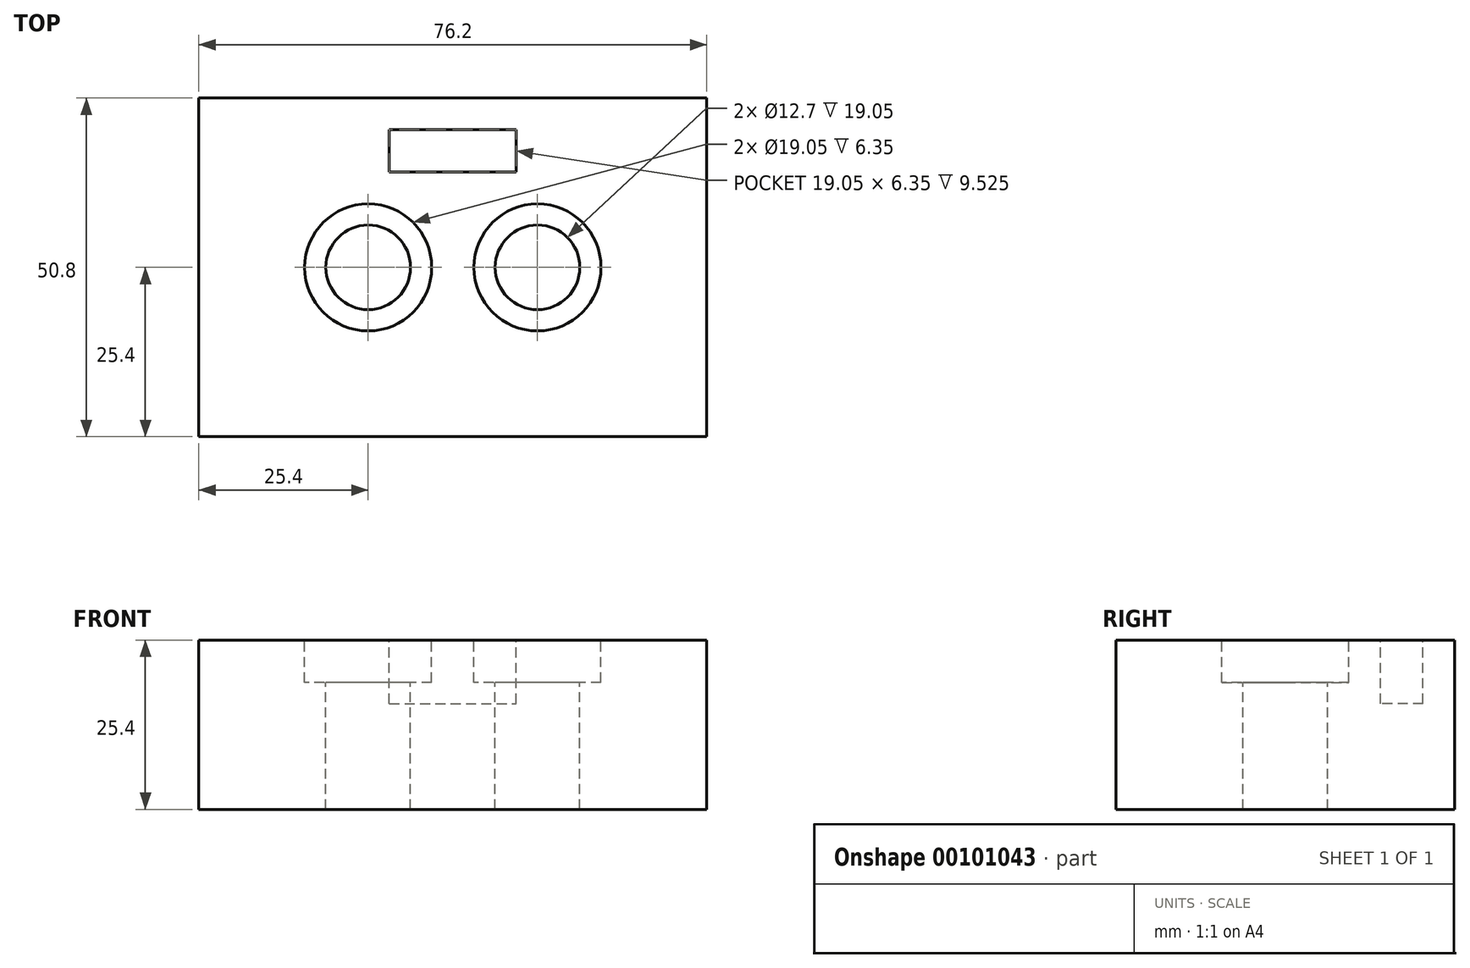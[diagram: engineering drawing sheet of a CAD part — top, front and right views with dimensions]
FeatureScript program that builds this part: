
annotation { "Feature Type Name" : "Feature", "Feature Type Description" : "" }
export const myFeature = defineFeature(function(context is Context, id is Id, definition is map)
    precondition{}
    {
        {
            var Q0;
            Q0=qCreatedBy(makeId("Front.planeOp"),FACE);
            var sketch = newSketch(context, id + "F0", { "sketchPlane" : qUnion([Q0])});
            skLineSegment(sketch, "E0.bottom", {"start": v(0, 0) * mm, "end": v(76.2, 0) * mm});
            skLineSegment(sketch, "E0.top", {"start": v(0, 25.4) * mm, "end": v(76.2, 25.4) * mm});
            skLineSegment(sketch, "E0.left", {"start": v(0, 0) * mm, "end": v(0, 25.4) * mm});
            skLineSegment(sketch, "E0.right", {"start": v(76.2, 0) * mm, "end": v(76.2, 25.4) * mm});
            skSolve(sketch);
        }
        {
            var Q0;
            Q0=makeQuery(id+"F0.imprint","IMPRINT",FACE,{"disambiguationData":[TD([[makeQuery(id+"F0.imprint","IMPRINT",EDGE,{"derivedFrom":sQuery(id+"F0.wireOp",EDGE,"E0.bottom")}),1.0]])]});
            extrude(context, id + "F1", {"entities" : qUnion([Q0]), "depth" : 50.8 * mm});
        }
        {
            var Q0;
            Q0=makeQuery(id+"F1.opExtrude","SWEPT_FACE",FACE,{"disambiguationData":[OSD([sQuery(id+"F0.wireOp",EDGE,"E0.top")])]});
            var sketch = newSketch(context, id + "F2", { "sketchPlane" : qUnion([Q0])});
            skPoint(sketch, "E1", {"position": v(25.4, -25.4) * mm});
            skPoint(sketch, "E2", {"position": v(50.8, -25.4) * mm});
            skSolve(sketch);
        }
        {
            var Q0;
            Q0=sQuery(id+"F2.wireOp",VERTEX,"E1");
            var Q1;
            Q1=sQuery(id+"F2.wireOp",VERTEX,"E2");
            var Q2;
            Q2=makeQuery(id+"F1.opExtrude","SWEPT_BODY",BODY,{"disambiguationData":[OSD([sQuery(id+"F0.wireOp",EDGE,"E0.bottom"),sQuery(id+"F0.wireOp",EDGE,"E0.top"),sQuery(id+"F0.wireOp",EDGE,"E0.left"),sQuery(id+"F0.wireOp",EDGE,"E0.right")])]});
            hole(context, id + "F3", {"style" : HoleStyle.C_BORE, "endStyle" : HoleEndStyle.THROUGH, "holeDiameter" : 12.7 * mm, "cBoreDiameter" : 19.05 * mm, "cBoreDepth" : 6.35 * mm, "startFromSketch" : true, "locations" : qUnion([Q0, Q1]), "scope" : qUnion([Q2]), "isTappedThrough" : true});
        }
        {
            var Q0;
            Q0=makeQuery(id+"F1.opExtrude","SWEPT_FACE",FACE,{"disambiguationData":[OSD([sQuery(id+"F0.wireOp",EDGE,"E0.top")])]});
            var sketch = newSketch(context, id + "F4", { "sketchPlane" : qUnion([Q0])});
            skLineSegment(sketch, "E3.bottom", {"start": v(28.58, -4.76) * mm, "end": v(47.62, -4.76) * mm});
            skLineSegment(sketch, "E3.top", {"start": v(28.58, -11.11) * mm, "end": v(47.62, -11.11) * mm});
            skLineSegment(sketch, "E3.left", {"start": v(28.58, -4.76) * mm, "end": v(28.58, -11.11) * mm});
            skLineSegment(sketch, "E3.right", {"start": v(47.62, -4.76) * mm, "end": v(47.62, -11.11) * mm});
            skSolve(sketch);
        }
        {
            var Q0;
            Q0=makeQuery(id+"F4.imprint","IMPRINT",FACE,{"disambiguationData":[TD([[makeQuery(id+"F4.imprint","IMPRINT",EDGE,{"derivedFrom":sQuery(id+"F4.wireOp",EDGE,"E3.bottom")}),-1.0]])]});
            extrude(context, id + "F5", {"entities" : qUnion([Q0]), "operationType" : NewBodyOperationType.REMOVE, "oppositeDirection" : true, "depth" : 9.52 * mm});
        }
    });
